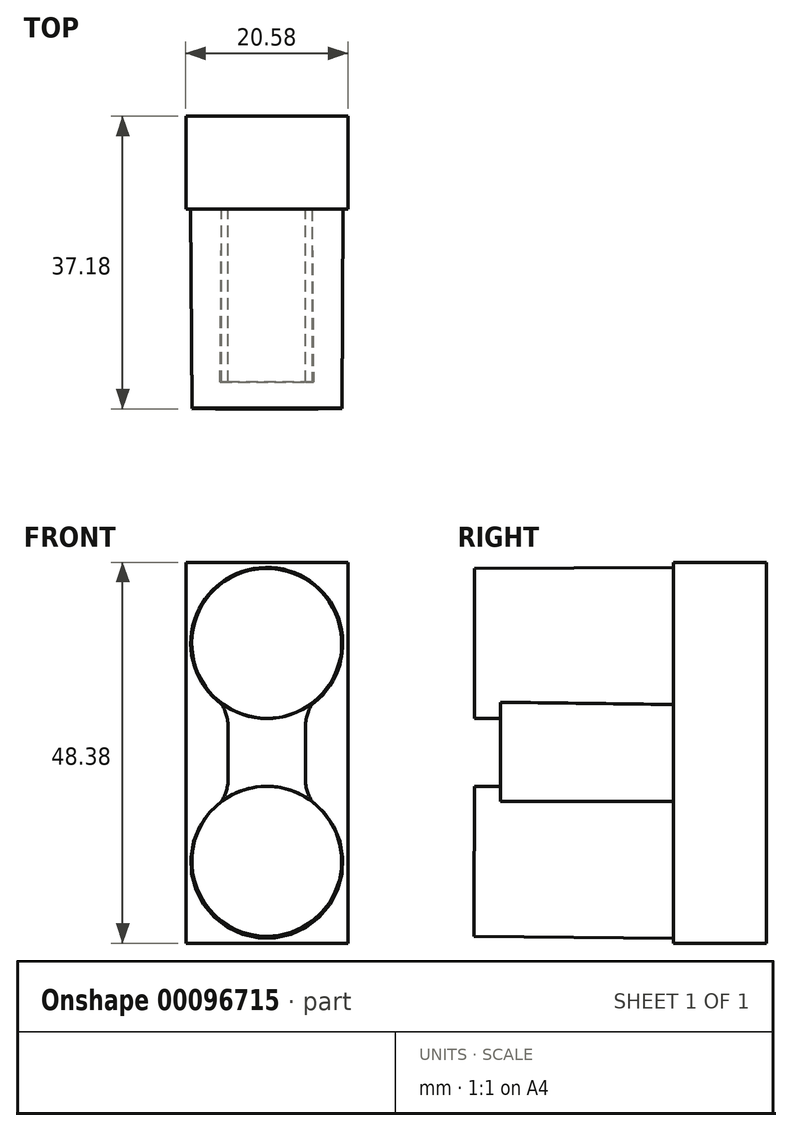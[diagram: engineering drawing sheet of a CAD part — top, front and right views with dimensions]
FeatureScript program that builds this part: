
annotation { "Feature Type Name" : "Feature", "Feature Type Description" : "" }
export const myFeature = defineFeature(function(context is Context, id is Id, definition is map)
    precondition{}
    {
        {
            var Q0;
            Q0=qCreatedBy(makeId("Right.planeOp"),FACE);
            var sketch = newSketch(context, id + "F0", { "sketchPlane" : qUnion([Q0])});
            skLineSegment(sketch, "E0", {"start": v(-25.4, 13.9) * mm, "end": v(0, 13.9) * mm});
            skLineSegment(sketch, "E1", {"start": v(-25.4, 13.9) * mm, "end": v(-25.4, 23.43) * mm});
            skLineSegment(sketch, "E2", {"start": v(0, -4.25) * mm, "end": v(-25.4, -4.25) * mm});
            skLineSegment(sketch, "E3", {"start": v(-25.4, -4.25) * mm, "end": v(-25.4, -13.78) * mm});
            skLineSegment(sketch, "E4", {"start": v(-25.4, -13.78) * mm, "end": v(0, -13.9) * mm});
            skLineSegment(sketch, "E5", {"start": v(0, -13.9) * mm, "end": v(0, -4.25) * mm});
            skLineSegment(sketch, "E6", {"start": v(0, -13.9) * mm, "end": v(0, -23.56) * mm});
            skLineSegment(sketch, "E7", {"start": v(-25.4, 13.9) * mm, "end": v(-25.4, 4.38) * mm});
            skLineSegment(sketch, "E8", {"start": v(-25.4, -13.78) * mm, "end": v(-25.4, -23.3) * mm});
            skLineSegment(sketch, "E9", {"start": v(-25.4, -23.3) * mm, "end": v(0, -23.56) * mm});
            skLineSegment(sketch, "E10", {"start": v(0, 23.56) * mm, "end": v(0, 13.9) * mm});
            skLineSegment(sketch, "E11", {"start": v(0, 13.9) * mm, "end": v(0, 4.25) * mm});
            skLineSegment(sketch, "E12", {"start": v(0, 4.25) * mm, "end": v(0, -4.25) * mm});
            skLineSegment(sketch, "E13", {"start": v(-25.4, 4.38) * mm, "end": v(0, 4.25) * mm});
            skLineSegment(sketch, "E14", {"start": v(-25.4, 23.43) * mm, "end": v(0, 23.56) * mm});
            skSolve(sketch);
        }
        {
            var Q0;
            Q0=makeQuery(id+"F0.imprint","IMPRINT",FACE,{"disambiguationData":[TD([[makeQuery(id+"F0.imprint","IMPRINT",EDGE,{"derivedFrom":sQuery(id+"F0.wireOp",EDGE,"E0")}),1.0]])]});
            var Q1;
            Q1=sQuery(id+"F0.wireOp",EDGE,"E0");
            revolve(context, id + "F1", {"entities" : qUnion([Q0]), "axis" : qUnion([Q1]), "revolveType" : RevolveType.FULL});
        }
        {
            var Q0;
            Q0=makeQuery(id+"F0.imprint","IMPRINT",FACE,{"disambiguationData":[TD([[makeQuery(id+"F0.imprint","IMPRINT",EDGE,{"derivedFrom":sQuery(id+"F0.wireOp",EDGE,"E2")}),1.0]])]});
            var Q1;
            Q1=sQuery(id+"F0.wireOp",EDGE,"E4");
            revolve(context, id + "F2", {"entities" : qUnion([Q0]), "axis" : qUnion([Q1]), "revolveType" : RevolveType.FULL});
        }
        {
            var Q0;
            Q0=qCreatedBy(makeId("Front.planeOp"),FACE);
            var sketch = newSketch(context, id + "F3", { "sketchPlane" : qUnion([Q0])});
            skLineSegment(sketch, "E15.bottom", {"start": v(10.29, 24.2) * mm, "end": v(-10.29, 24.2) * mm});
            skLineSegment(sketch, "E15.top", {"start": v(10.29, -24.2) * mm, "end": v(-10.29, -24.2) * mm});
            skLineSegment(sketch, "E15.left", {"start": v(10.29, 24.2) * mm, "end": v(10.29, -24.2) * mm});
            skLineSegment(sketch, "E15.right", {"start": v(-10.29, 24.2) * mm, "end": v(-10.29, -24.2) * mm});
            skPoint(sketch, "E16", {"position": v(-9.65, 13.9) * mm});
            skPoint(sketch, "E17", {"position": v(0, 24.2) * mm});
            skLineSegment(sketch, "E18", {"start": v(4.89, 3.17) * mm, "end": v(4.89, -3.17) * mm});
            skLineSegment(sketch, "E19", {"start": v(-4.89, 3.18) * mm, "end": v(-4.89, -3.18) * mm});
            skPoint(sketch, "E20", {"position": v(4.89, 0) * mm});
            skPoint(sketch, "E21", {"position": v(-4.89, 0) * mm});
            skLineSegment(sketch, "E22", {"start": v(4.89, 0) * mm, "end": v(-4.89, 0) * mm, "construction": true});
            skPoint(sketch, "E23", {"position": v(0, 0) * mm});
            skCircle(sketch, "E24", {"center": v(0, -13.9) * mm, "radius": 9.4 * mm});
            skCircle(sketch, "E25", {"center": v(0, 13.9) * mm, "radius": 9.4 * mm});
            skArc(sketch, "E26", {"start": v(6.58, 7.2) * mm, "mid": v(5.33, 5.35) * mm, "end": v(4.89, 3.17) * mm});
            skArc(sketch, "E27", {"start": v(4.89, -3.18) * mm, "mid": v(5.33, -5.35) * mm, "end": v(6.58, -7.2) * mm});
            skArc(sketch, "E28", {"start": v(-6.58, -7.2) * mm, "mid": v(-5.33, -5.35) * mm, "end": v(-4.89, -3.18) * mm});
            skArc(sketch, "E29", {"start": v(-4.89, 3.18) * mm, "mid": v(-5.33, 5.35) * mm, "end": v(-6.58, 7.2) * mm});
            skSolve(sketch);
        }
        {
            var Q0;
            Q0=makeQuery(id+"F3.imprint","IMPRINT",FACE,{"disambiguationData":[TD([[makeQuery(id+"F3.imprint","IMPRINT",EDGE,{"derivedFrom":sQuery(id+"F3.wireOp",EDGE,"E18")}),-1.0]])]});
            extrude(context, id + "F4", {"entities" : qUnion([Q0]), "operationType" : NewBodyOperationType.ADD, "depth" : 22.1 * mm});
        }
        {
            var Q0;
            Q0 = qSketchRegion(id + "F3", true);
            var Q1;
            {var subQ0=sQuery(id+"F3.wireOp",EDGE,"E24");var subQ1=makeQuery(id+"F3.imprint","INTERSECT",VERTEX,{"derivedFrom":[subQ0,sQuery(id+"F3.wireOp",EDGE,"E27")]});Q1=makeQuery(id+"F3.imprint","IMPRINT",FACE,{"disambiguationData":[TD([[makeQuery(id+"F3.imprint","IMPRINT",EDGE,{"disambiguationData":[TD([[subQ1,-1.0]])],"derivedFrom":subQ0}),1.0]])]});}
            var Q2;
            Q2=makeQuery(id+"F3.imprint","IMPRINT",FACE,{"disambiguationData":[TD([[makeQuery(id+"F3.imprint","IMPRINT",EDGE,{"derivedFrom":sQuery(id+"F3.wireOp",EDGE,"E18")}),-1.0]])]});
            var Q3;
            {var subQ0=sQuery(id+"F3.wireOp",EDGE,"E25");var subQ1=makeQuery(id+"F3.imprint","INTERSECT",VERTEX,{"derivedFrom":[subQ0,sQuery(id+"F3.wireOp",EDGE,"E26")]});Q3=makeQuery(id+"F3.imprint","IMPRINT",FACE,{"disambiguationData":[TD([[makeQuery(id+"F3.imprint","IMPRINT",EDGE,{"disambiguationData":[TD([[subQ1,1.0]])],"derivedFrom":subQ0}),1.0]])]});}
            extrude(context, id + "F5", {"entities" : qUnion([Q0, Q1, Q2, Q3]), "operationType" : NewBodyOperationType.ADD, "endBound" : BoundingType.SYMMETRIC, "oppositeDirection" : true, "depth" : 0.25 * mm});
        }
        {
            var Q0;
            Q0=makeQuery(id+"F5.opExtrude","CAP_FACE",FACE,{"disambiguationData":[OSD([sQuery(id+"F3.wireOp",EDGE,"E15.bottom"),sQuery(id+"F3.wireOp",EDGE,"E15.top"),sQuery(id+"F3.wireOp",EDGE,"E15.left"),sQuery(id+"F3.wireOp",EDGE,"E15.right")])],"isStart":false});
            var Q1;
            Q1=sQuery(id+"F3.wireOp",EDGE,"E15.top");
            extrude(context, id + "F6", {"entities" : qUnion([Q0]), "operationType" : NewBodyOperationType.ADD, "surfaceEntities" : qUnion([Q1]), "depth" : 11.56 * mm});
        }
    });
